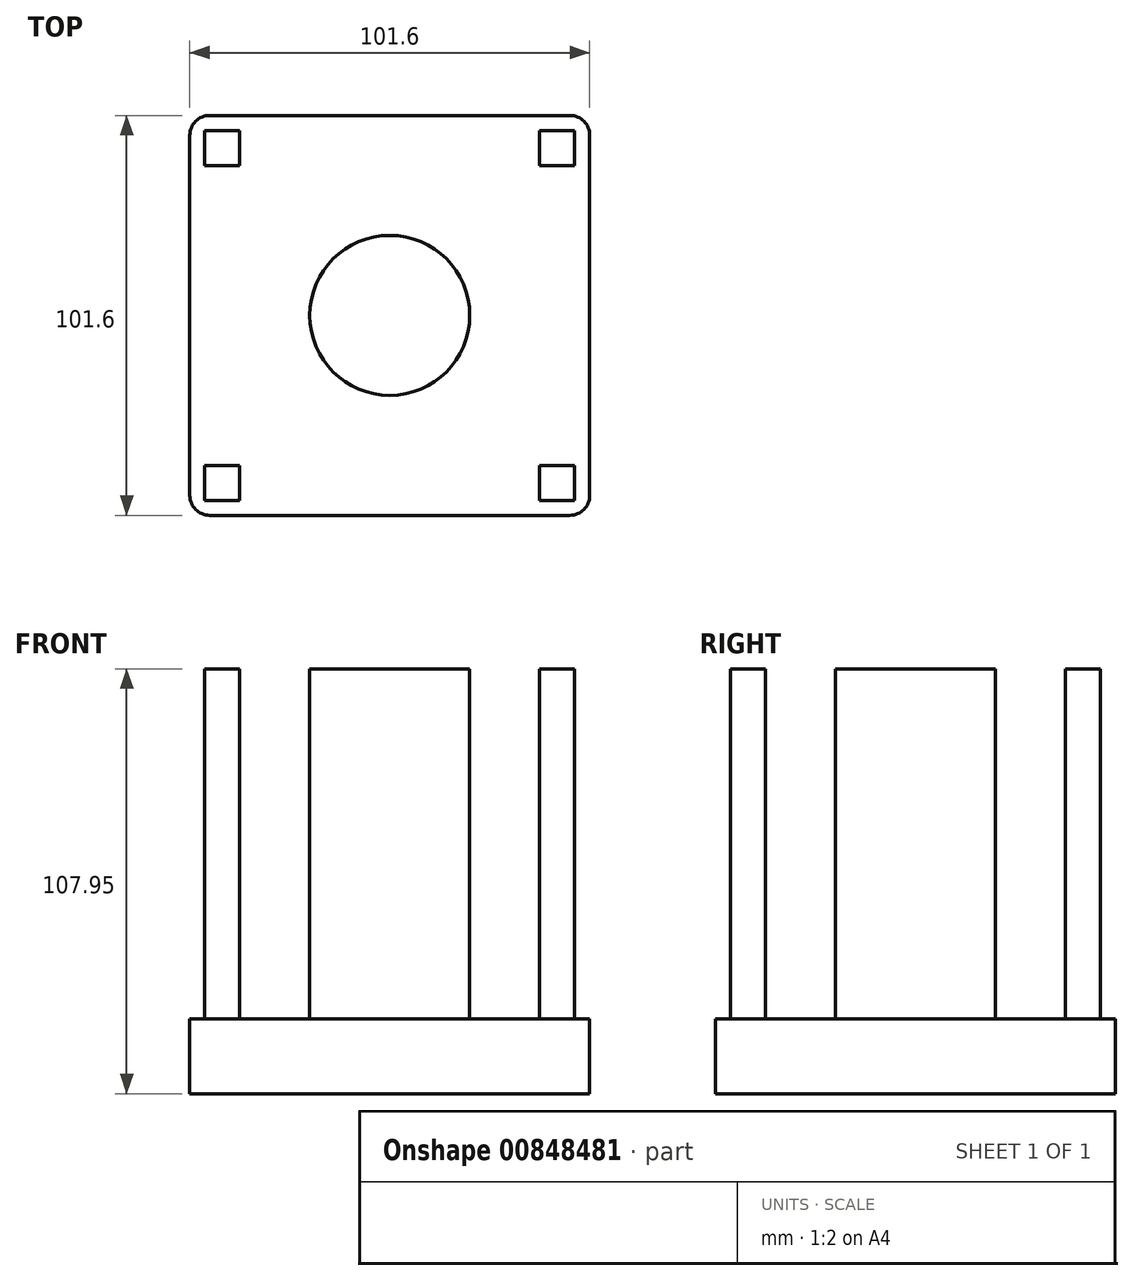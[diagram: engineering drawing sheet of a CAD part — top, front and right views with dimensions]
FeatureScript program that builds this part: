
annotation { "Feature Type Name" : "Feature", "Feature Type Description" : "" }
export const myFeature = defineFeature(function(context is Context, id is Id, definition is map)
    precondition{}
    {
        {
            var Q0;
            Q0=qCreatedBy(makeId("Top.planeOp"),FACE);
            var sketch = newSketch(context, id + "F0", { "sketchPlane" : qUnion([Q0])});
            skLineSegment(sketch, "E0.bottom", {"start": v(50.8, -50.8) * mm, "end": v(-50.8, -50.8) * mm});
            skLineSegment(sketch, "E0.top", {"start": v(50.8, 50.8) * mm, "end": v(-50.8, 50.8) * mm});
            skLineSegment(sketch, "E0.left", {"start": v(50.8, -50.8) * mm, "end": v(50.8, 50.8) * mm});
            skLineSegment(sketch, "E0.right", {"start": v(-50.8, -50.8) * mm, "end": v(-50.8, 50.8) * mm});
            skPoint(sketch, "E0.middle", {"position": v(0, 0) * mm});
            skSolve(sketch);
        }
        {
            var Q0;
            Q0=makeQuery(id+"F0.imprint","IMPRINT",FACE,{"disambiguationData":[TD([[makeQuery(id+"F0.imprint","IMPRINT",EDGE,{"derivedFrom":sQuery(id+"F0.wireOp",EDGE,"E0.bottom")}),-1.0]])]});
            extrude(context, id + "F1", {"entities" : qUnion([Q0]), "oppositeDirection" : true, "depth" : 19.05 * mm, "offsetDistance" : 25.4 * mm});
        }
        {
            var Q0;
            Q0=makeQuery(id+"F1.opExtrude","CAP_FACE",FACE,{"disambiguationData":[OSD([sQuery(id+"F0.wireOp",EDGE,"E0.bottom"),sQuery(id+"F0.wireOp",EDGE,"E0.top"),sQuery(id+"F0.wireOp",EDGE,"E0.left"),sQuery(id+"F0.wireOp",EDGE,"E0.right")])],"isStart":true});
            var sketch = newSketch(context, id + "F2", { "sketchPlane" : qUnion([Q0])});
            skLineSegment(sketch, "E1.bottom", {"start": v(38.1, -38.1) * mm, "end": v(47, -38.1) * mm});
            skLineSegment(sketch, "E1.top", {"start": v(38.1, -46.99) * mm, "end": v(47, -46.99) * mm});
            skLineSegment(sketch, "E1.left", {"start": v(38.1, -38.1) * mm, "end": v(38.1, -46.99) * mm});
            skLineSegment(sketch, "E1.right", {"start": v(47, -38.1) * mm, "end": v(47, -46.99) * mm});
            skPoint(sketch, "E1.middle", {"position": v(42.55, -42.55) * mm});
            skLineSegment(sketch, "E2.bottom", {"start": v(-46.99, -38.1) * mm, "end": v(-38.1, -38.1) * mm});
            skLineSegment(sketch, "E2.top", {"start": v(-46.99, -47) * mm, "end": v(-38.1, -47) * mm});
            skLineSegment(sketch, "E2.left", {"start": v(-46.99, -38.1) * mm, "end": v(-46.99, -47) * mm});
            skLineSegment(sketch, "E2.right", {"start": v(-38.1, -38.1) * mm, "end": v(-38.1, -47) * mm});
            skPoint(sketch, "E2.middle", {"position": v(-42.54, -42.55) * mm});
            skLineSegment(sketch, "E3.bottom", {"start": v(38.1, 47) * mm, "end": v(46.99, 47) * mm});
            skLineSegment(sketch, "E3.top", {"start": v(38.1, 38.1) * mm, "end": v(46.99, 38.1) * mm});
            skLineSegment(sketch, "E3.left", {"start": v(38.1, 47) * mm, "end": v(38.1, 38.1) * mm});
            skLineSegment(sketch, "E3.right", {"start": v(46.99, 47) * mm, "end": v(46.99, 38.1) * mm});
            skPoint(sketch, "E3.middle", {"position": v(42.55, 42.55) * mm});
            skLineSegment(sketch, "E4.bottom", {"start": v(-47, 47) * mm, "end": v(-38.1, 47) * mm});
            skLineSegment(sketch, "E4.top", {"start": v(-47, 38.1) * mm, "end": v(-38.1, 38.1) * mm});
            skLineSegment(sketch, "E4.left", {"start": v(-47, 47) * mm, "end": v(-47, 38.1) * mm});
            skLineSegment(sketch, "E4.right", {"start": v(-38.1, 47) * mm, "end": v(-38.1, 38.1) * mm});
            skPoint(sketch, "E4.middle", {"position": v(-42.55, 42.55) * mm});
            skLineSegment(sketch, "E5.bottom", {"start": v(38.1, 4.45) * mm, "end": v(47, 4.45) * mm});
            skLineSegment(sketch, "E5.top", {"start": v(38.1, -4.44) * mm, "end": v(47, -4.44) * mm});
            skLineSegment(sketch, "E5.left", {"start": v(38.1, 4.45) * mm, "end": v(38.1, -4.44) * mm});
            skLineSegment(sketch, "E5.right", {"start": v(46.99, 4.45) * mm, "end": v(47, -4.44) * mm});
            skPoint(sketch, "E5.middle", {"position": v(42.55, 0) * mm});
            skLineSegment(sketch, "E6.bottom", {"start": v(-4.44, -38.1) * mm, "end": v(4.45, -38.1) * mm});
            skLineSegment(sketch, "E6.top", {"start": v(-4.44, -47) * mm, "end": v(4.45, -47) * mm});
            skLineSegment(sketch, "E6.left", {"start": v(-4.44, -38.1) * mm, "end": v(-4.44, -47) * mm});
            skLineSegment(sketch, "E6.right", {"start": v(4.45, -38.1) * mm, "end": v(4.45, -47) * mm});
            skPoint(sketch, "E6.middle", {"position": v(0, -42.55) * mm});
            skLineSegment(sketch, "E7.bottom", {"start": v(-47, 4.45) * mm, "end": v(-38.1, 4.45) * mm});
            skLineSegment(sketch, "E7.top", {"start": v(-47, -4.44) * mm, "end": v(-38.1, -4.44) * mm});
            skLineSegment(sketch, "E7.left", {"start": v(-47, 4.45) * mm, "end": v(-47, -4.44) * mm});
            skLineSegment(sketch, "E7.right", {"start": v(-38.1, 4.45) * mm, "end": v(-38.1, -4.44) * mm});
            skPoint(sketch, "E7.middle", {"position": v(-42.54, 0) * mm});
            skLineSegment(sketch, "E8.bottom", {"start": v(-4.45, 47) * mm, "end": v(4.44, 47) * mm});
            skLineSegment(sketch, "E8.top", {"start": v(-4.45, 38.1) * mm, "end": v(4.44, 38.1) * mm});
            skLineSegment(sketch, "E8.left", {"start": v(-4.45, 47) * mm, "end": v(-4.45, 38.1) * mm});
            skLineSegment(sketch, "E8.right", {"start": v(4.44, 47) * mm, "end": v(4.44, 38.1) * mm});
            skPoint(sketch, "E8.middle", {"position": v(0, 42.55) * mm});
            skLineSegment(sketch, "E9", {"start": v(57.35, 0) * mm, "end": v(-62.24, 0) * mm, "construction": true});
            skLineSegment(sketch, "E10", {"start": v(0, -68.69) * mm, "end": v(0, 73.73) * mm, "construction": true});
            skLineSegment(sketch, "E11.bottom", {"start": v(-44.68, -38.1) * mm, "end": v(-44.17, -38.1) * mm});
            skLineSegment(sketch, "E11.top", {"start": v(-44.68, 38.1) * mm, "end": v(-44.17, 38.1) * mm});
            skLineSegment(sketch, "E12", {"start": v(-42.54, -42.55) * mm, "end": v(-42.55, 42.55) * mm, "construction": true});
            skLineSegment(sketch, "E13.bottom", {"start": v(42.3, -38.1) * mm, "end": v(42.8, -38.1) * mm});
            skLineSegment(sketch, "E13.top", {"start": v(42.3, 38.1) * mm, "end": v(42.8, 38.1) * mm});
            skLineSegment(sketch, "E13.left", {"start": v(42.3, -38.1) * mm, "end": v(42.3, 38.1) * mm});
            skLineSegment(sketch, "E13.right", {"start": v(42.8, -38.1) * mm, "end": v(42.8, 38.1) * mm});
            skLineSegment(sketch, "E14.bottom", {"start": v(-42.8, -38.1) * mm, "end": v(-42.3, -38.1) * mm});
            skLineSegment(sketch, "E14.top", {"start": v(-42.8, 38.1) * mm, "end": v(-42.3, 38.1) * mm});
            skLineSegment(sketch, "E14.left", {"start": v(-42.8, -38.1) * mm, "end": v(-42.8, 38.1) * mm});
            skLineSegment(sketch, "E14.right", {"start": v(-42.3, -38.1) * mm, "end": v(-42.3, 38.1) * mm});
            skLineSegment(sketch, "E15.bottom", {"start": v(-38.1, 42.3) * mm, "end": v(38.1, 42.3) * mm});
            skLineSegment(sketch, "E15.top", {"start": v(-38.1, 42.8) * mm, "end": v(38.1, 42.8) * mm});
            skLineSegment(sketch, "E15.left", {"start": v(-38.1, 42.3) * mm, "end": v(-38.1, 42.8) * mm});
            skLineSegment(sketch, "E15.right", {"start": v(38.1, 42.3) * mm, "end": v(38.1, 42.8) * mm});
            skLineSegment(sketch, "E16.bottom", {"start": v(-38.1, -42.8) * mm, "end": v(38.1, -42.8) * mm});
            skLineSegment(sketch, "E16.top", {"start": v(-38.1, -42.3) * mm, "end": v(38.1, -42.3) * mm});
            skLineSegment(sketch, "E16.left", {"start": v(-38.1, -42.8) * mm, "end": v(-38.1, -42.3) * mm});
            skLineSegment(sketch, "E16.right", {"start": v(38.1, -42.8) * mm, "end": v(38.1, -42.3) * mm});
            skSolve(sketch);
        }
        {
            var Q0;
            Q0=makeQuery(id+"F2.imprint","IMPRINT",FACE,{"disambiguationData":[TD([[makeQuery(id+"F2.imprint","IMPRINT",EDGE,{"derivedFrom":sQuery(id+"F2.wireOp",EDGE,"E1.bottom")}),-1.0]])]});
            var Q1;
            Q1=makeQuery(id+"F2.imprint","IMPRINT",FACE,{"disambiguationData":[TD([[makeQuery(id+"F2.imprint","IMPRINT",EDGE,{"derivedFrom":sQuery(id+"F2.wireOp",EDGE,"E2.bottom")}),-1.0]])]});
            var Q2;
            Q2=makeQuery(id+"F2.imprint","IMPRINT",FACE,{"disambiguationData":[TD([[makeQuery(id+"F2.imprint","IMPRINT",EDGE,{"derivedFrom":sQuery(id+"F2.wireOp",EDGE,"E4.bottom")}),-1.0]])]});
            var Q3;
            Q3=makeQuery(id+"F2.imprint","IMPRINT",FACE,{"disambiguationData":[TD([[makeQuery(id+"F2.imprint","IMPRINT",EDGE,{"derivedFrom":sQuery(id+"F2.wireOp",EDGE,"E3.bottom")}),-1.0]])]});
            extrude(context, id + "F3", {"entities" : qUnion([Q0, Q1, Q2, Q3]), "depth" : 88.9 * mm, "offsetDistance" : 25.4 * mm});
        }
        {
            var Q0;
            Q0=makeQuery(id+"F1.opExtrude","CAP_FACE",FACE,{"disambiguationData":[OSD([sQuery(id+"F0.wireOp",EDGE,"E0.bottom"),sQuery(id+"F0.wireOp",EDGE,"E0.top"),sQuery(id+"F0.wireOp",EDGE,"E0.left"),sQuery(id+"F0.wireOp",EDGE,"E0.right")])],"isStart":true});
            var sketch = newSketch(context, id + "F4", { "sketchPlane" : qUnion([Q0])});
            skCircle(sketch, "E17", {"center": v(0, 0) * mm, "radius": 20.32 * mm});
            skSolve(sketch);
        }
        {
            var Q0;
            Q0=makeQuery(id+"F4.imprint","IMPRINT",FACE,{"disambiguationData":[TD([[makeQuery(id+"F4.imprint","IMPRINT",EDGE,{"derivedFrom":sQuery(id+"F4.wireOp",EDGE,"E17")}),1.0]])]});
            extrude(context, id + "F5", {"entities" : qUnion([Q0]), "depth" : 88.9 * mm, "offsetDistance" : 25.4 * mm});
        }
        {
            var Q0;
            Q0=makeQuery(id+"F1.opExtrude","SWEPT_EDGE",EDGE,{"disambiguationData":[OSD([sQuery(id+"F0.wireOp",EDGE,"E0.top"),sQuery(id+"F0.wireOp",EDGE,"E0.right")])]});
            fillet(context, id + "F6", {"entities" : qUnion([Q0]), "radius" : 5.08 * mm, "tangentPropagation" : true, "allowEdgeOverflow" : false});
        }
        {
            var Q0;
            Q0=makeQuery(id+"F1.opExtrude","SWEPT_EDGE",EDGE,{"disambiguationData":[OSD([sQuery(id+"F0.wireOp",EDGE,"E0.top"),sQuery(id+"F0.wireOp",EDGE,"E0.left")])]});
            fillet(context, id + "F7", {"entities" : qUnion([Q0]), "radius" : 5.08 * mm, "tangentPropagation" : true, "allowEdgeOverflow" : false});
        }
        {
            var Q0;
            Q0=makeQuery(id+"F1.opExtrude","SWEPT_EDGE",EDGE,{"disambiguationData":[OSD([sQuery(id+"F0.wireOp",EDGE,"E0.bottom"),sQuery(id+"F0.wireOp",EDGE,"E0.left")])]});
            fillet(context, id + "F8", {"entities" : qUnion([Q0]), "radius" : 5.08 * mm, "tangentPropagation" : true, "allowEdgeOverflow" : false});
        }
        {
            var Q0;
            Q0=makeQuery(id+"F1.opExtrude","SWEPT_EDGE",EDGE,{"disambiguationData":[OSD([sQuery(id+"F0.wireOp",EDGE,"E0.bottom"),sQuery(id+"F0.wireOp",EDGE,"E0.right")])]});
            fillet(context, id + "F9", {"entities" : qUnion([Q0]), "radius" : 5.08 * mm, "tangentPropagation" : true, "allowEdgeOverflow" : false});
        }
        {
            var Q0;
            Q0=sQuery(id+"F2.wireOp",EDGE,"E14.left");
            var Q1;
            Q1=sQuery(id+"F2.wireOp",EDGE,"E14.right");
            var Q2;
            Q2=sQuery(id+"F2.wireOp",EDGE,"E14.top");
            var Q3;
            Q3=sQuery(id+"F2.wireOp",EDGE,"E16.left");
            var Q4;
            Q4=sQuery(id+"F2.wireOp",EDGE,"E16.bottom");
            var Q5;
            Q5=sQuery(id+"F2.wireOp",EDGE,"E16.top");
            var Q6;
            Q6=sQuery(id+"F2.wireOp",EDGE,"E13.left");
            var Q7;
            Q7=sQuery(id+"F2.wireOp",EDGE,"E13.right");
            var Q8;
            Q8=sQuery(id+"F2.wireOp",EDGE,"E13.bottom");
            var Q9;
            Q9=sQuery(id+"F2.wireOp",EDGE,"E15.bottom");
            var Q10;
            Q10=sQuery(id+"F2.wireOp",EDGE,"E15.top");
            var Q11;
            Q11=sQuery(id+"F2.wireOp",EDGE,"E15.right");
            extrude(context, id + "F10", {"bodyType" : ToolBodyType.SURFACE, "surfaceEntities" : qUnion([Q0, Q1, Q2, Q3, Q4, Q5, Q6, Q7, Q8, Q9, Q10, Q11]), "depth" : 83.82 * mm, "offsetDistance" : 25.4 * mm});
        }
    });
